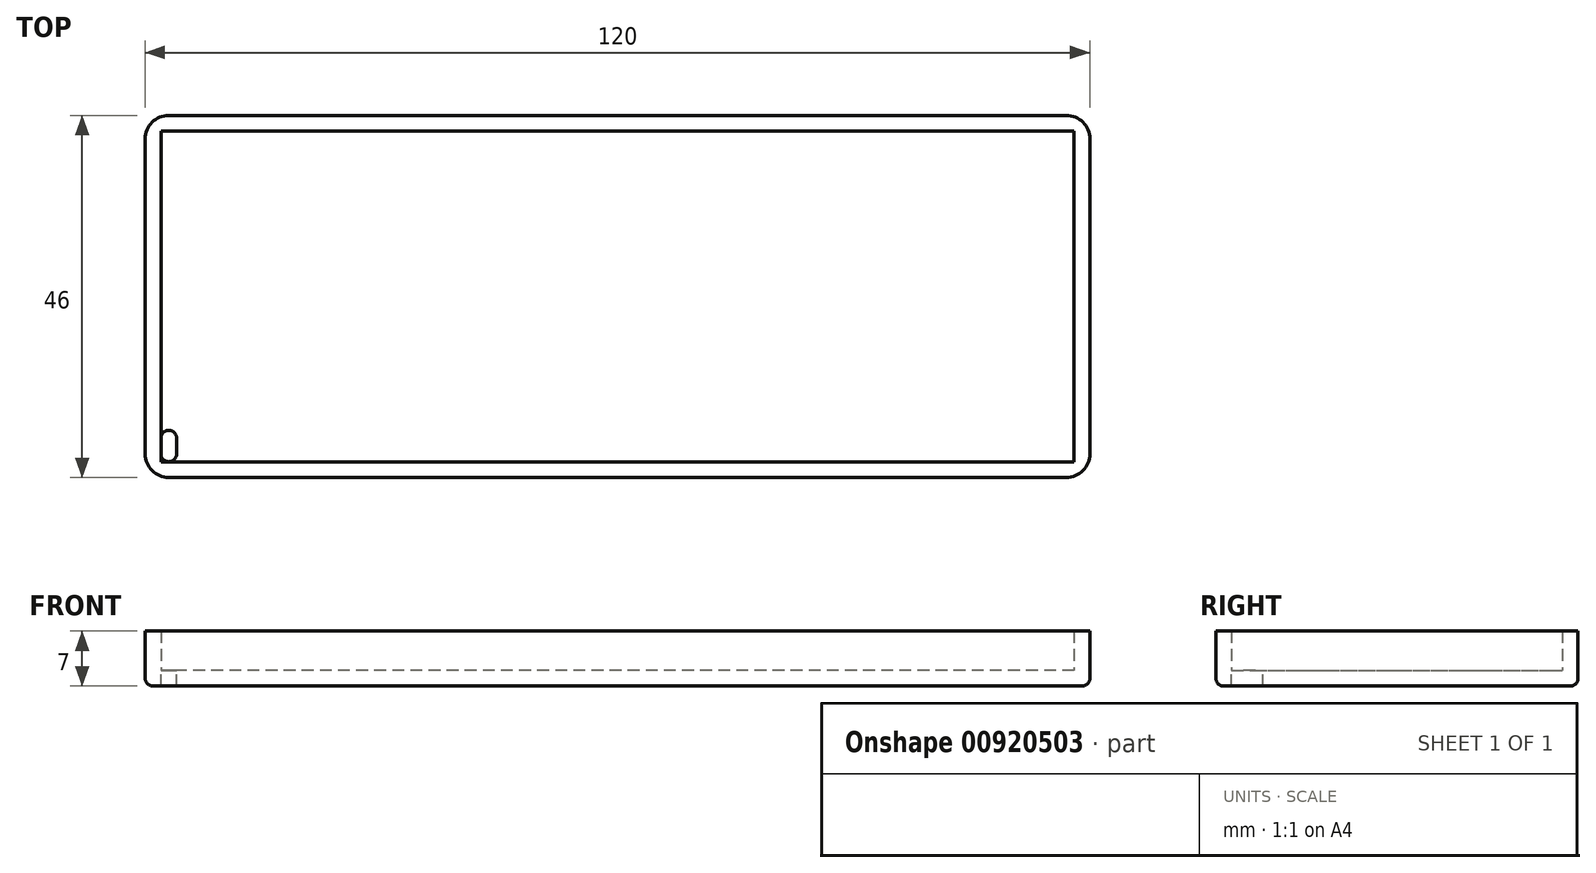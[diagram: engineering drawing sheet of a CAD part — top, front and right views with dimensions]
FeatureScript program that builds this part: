
annotation { "Feature Type Name" : "Feature", "Feature Type Description" : "" }
export const myFeature = defineFeature(function(context is Context, id is Id, definition is map)
    precondition{}
    {
        {
            var Q0;
            Q0=qCreatedBy(makeId("Top.planeOp"),FACE);
            var sketch = newSketch(context, id + "F0", { "sketchPlane" : qUnion([Q0])});
            skLineSegment(sketch, "E0.bottom", {"start": v(60, -23) * mm, "end": v(-60, -23) * mm});
            skLineSegment(sketch, "E0.top", {"start": v(60, 23) * mm, "end": v(-60, 23) * mm});
            skLineSegment(sketch, "E0.left", {"start": v(60, -23) * mm, "end": v(60, 23) * mm});
            skLineSegment(sketch, "E0.right", {"start": v(-60, -23) * mm, "end": v(-60, 23) * mm});
            skPoint(sketch, "E0.middle", {"position": v(0, 0) * mm});
            skSolve(sketch);
        }
        {
            var Q0;
            Q0=makeQuery(id+"F0.imprint","IMPRINT",FACE,{"disambiguationData":[TD([[makeQuery(id+"F0.imprint","IMPRINT",EDGE,{"derivedFrom":sQuery(id+"F0.wireOp",EDGE,"E0.bottom")}),-1.0]])]});
            extrude(context, id + "F1", {"entities" : qUnion([Q0]), "depth" : 2 * mm, "offsetDistance" : 25 * mm});
        }
        {
            var Q0;
            Q0=makeQuery(id+"F1.opExtrude","CAP_FACE",FACE,{"disambiguationData":[OSD([sQuery(id+"F0.wireOp",EDGE,"E0.bottom"),sQuery(id+"F0.wireOp",EDGE,"E0.top"),sQuery(id+"F0.wireOp",EDGE,"E0.left"),sQuery(id+"F0.wireOp",EDGE,"E0.right")])],"isStart":false});
            var sketch = newSketch(context, id + "F2", { "sketchPlane" : qUnion([Q0])});
            skLineSegment(sketch, "E1.bottom", {"start": v(58, -21) * mm, "end": v(-58, -21) * mm});
            skLineSegment(sketch, "E1.top", {"start": v(58, 21) * mm, "end": v(-58, 21) * mm});
            skLineSegment(sketch, "E1.left", {"start": v(58, -21) * mm, "end": v(58, 21) * mm});
            skLineSegment(sketch, "E1.right", {"start": v(-58, -21) * mm, "end": v(-58, 21) * mm});
            skPoint(sketch, "E1.middle", {"position": v(0, 0) * mm});
            skCircle(sketch, "E2", {"center": v(-57, -20) * mm, "radius": 1 * mm});
            skCircle(sketch, "E3", {"center": v(-57, -18) * mm, "radius": 1 * mm});
            skLineSegment(sketch, "E4", {"start": v(-56, -18) * mm, "end": v(-56, -20) * mm});
            skSolve(sketch);
        }
        {
            var Q0;
            Q0=makeQuery(id+"F2.imprint","IMPRINT",FACE,{"disambiguationData":[TD([[makeQuery(id+"F2.imprint","IMPRINT",EDGE,{"derivedFrom":sQuery(id+"F2.wireOp",EDGE,"E1.bottom")}),1.0]])]});
            extrude(context, id + "F3", {"entities" : qUnion([Q0]), "operationType" : NewBodyOperationType.ADD, "depth" : 5 * mm, "offsetDistance" : 25 * mm});
        }
        {
            var Q0;
            {var subQ0=sQuery(id+"F0.wireOp",EDGE,"E0.right");var subQ1=sQuery(id+"F0.wireOp",EDGE,"E0.top");Q0=makeQuery(id+"F3.boolean.opBoolean","MERGE",EDGE,{"derivedFrom":[makeQuery(id+"F1.opExtrude","SWEPT_EDGE",EDGE,{"disambiguationData":[OSD([subQ1,subQ0])]}),makeQuery(id+"F3.opExtrude","SWEPT_EDGE",EDGE,{"disambiguationData":[OSD([subQ1,subQ0])]})]});}
            var Q1;
            {var subQ0=sQuery(id+"F0.wireOp",EDGE,"E0.right");var subQ1=sQuery(id+"F0.wireOp",EDGE,"E0.bottom");Q1=makeQuery(id+"F3.boolean.opBoolean","MERGE",EDGE,{"derivedFrom":[makeQuery(id+"F1.opExtrude","SWEPT_EDGE",EDGE,{"disambiguationData":[OSD([subQ1,subQ0])]}),makeQuery(id+"F3.opExtrude","SWEPT_EDGE",EDGE,{"disambiguationData":[OSD([subQ1,subQ0])]})]});}
            var Q2;
            {var subQ0=sQuery(id+"F0.wireOp",EDGE,"E0.left");var subQ1=sQuery(id+"F0.wireOp",EDGE,"E0.top");Q2=makeQuery(id+"F3.boolean.opBoolean","MERGE",EDGE,{"derivedFrom":[makeQuery(id+"F1.opExtrude","SWEPT_EDGE",EDGE,{"disambiguationData":[OSD([subQ1,subQ0])]}),makeQuery(id+"F3.opExtrude","SWEPT_EDGE",EDGE,{"disambiguationData":[OSD([subQ1,subQ0])]})]});}
            var Q3;
            {var subQ0=sQuery(id+"F0.wireOp",EDGE,"E0.left");var subQ1=sQuery(id+"F0.wireOp",EDGE,"E0.bottom");Q3=makeQuery(id+"F3.boolean.opBoolean","MERGE",EDGE,{"derivedFrom":[makeQuery(id+"F1.opExtrude","SWEPT_EDGE",EDGE,{"disambiguationData":[OSD([subQ1,subQ0])]}),makeQuery(id+"F3.opExtrude","SWEPT_EDGE",EDGE,{"disambiguationData":[OSD([subQ1,subQ0])]})]});}
            fillet(context, id + "F4", {"entities" : qUnion([Q0, Q1, Q2, Q3]), "radius" : 3 * mm, "tangentPropagation" : true, "allowEdgeOverflow" : false});
        }
        {
            var Q0;
            Q0=makeQuery(id+"F1.opExtrude","CAP_EDGE",EDGE,{"disambiguationData":[OSD([sQuery(id+"F0.wireOp",EDGE,"E0.top")])],"isStart":true});
            var Q1;
            {var subQ0=sQuery(id+"F0.wireOp",EDGE,"E0.right");var subQ1=sQuery(id+"F0.wireOp",EDGE,"E0.top");Q1=makeQuery(id+"F4.opFillet","BLEND_EDGE",EDGE,{"blendedFrom":[makeQuery(id+"F3.boolean.opBoolean","MERGE",EDGE,{"derivedFrom":[makeQuery(id+"F1.opExtrude","SWEPT_EDGE",EDGE,{"disambiguationData":[OSD([subQ1,subQ0])]}),makeQuery(id+"F3.opExtrude","SWEPT_EDGE",EDGE,{"disambiguationData":[OSD([subQ1,subQ0])]})]}),makeQuery(id+"F1.opExtrude","CAP_FACE",FACE,{"disambiguationData":[OSD([sQuery(id+"F0.wireOp",EDGE,"E0.bottom"),subQ1,sQuery(id+"F0.wireOp",EDGE,"E0.left"),subQ0])],"isStart":true})],"blendedInto":[makeQuery(id+"F1.opExtrude","CAP_FACE",FACE,{"disambiguationData":[OSD([sQuery(id+"F0.wireOp",EDGE,"E0.bottom"),subQ1,sQuery(id+"F0.wireOp",EDGE,"E0.left"),subQ0])],"isStart":true})]});}
            var Q2;
            Q2=makeQuery(id+"F1.opExtrude","CAP_EDGE",EDGE,{"disambiguationData":[OSD([sQuery(id+"F0.wireOp",EDGE,"E0.right")])],"isStart":true});
            var Q3;
            {var subQ0=sQuery(id+"F0.wireOp",EDGE,"E0.right");var subQ1=sQuery(id+"F0.wireOp",EDGE,"E0.bottom");Q3=makeQuery(id+"F4.opFillet","BLEND_EDGE",EDGE,{"blendedFrom":[makeQuery(id+"F3.boolean.opBoolean","MERGE",EDGE,{"derivedFrom":[makeQuery(id+"F1.opExtrude","SWEPT_EDGE",EDGE,{"disambiguationData":[OSD([subQ1,subQ0])]}),makeQuery(id+"F3.opExtrude","SWEPT_EDGE",EDGE,{"disambiguationData":[OSD([subQ1,subQ0])]})]}),makeQuery(id+"F1.opExtrude","CAP_FACE",FACE,{"disambiguationData":[OSD([subQ1,sQuery(id+"F0.wireOp",EDGE,"E0.top"),sQuery(id+"F0.wireOp",EDGE,"E0.left"),subQ0])],"isStart":true})],"blendedInto":[makeQuery(id+"F1.opExtrude","CAP_FACE",FACE,{"disambiguationData":[OSD([subQ1,sQuery(id+"F0.wireOp",EDGE,"E0.top"),sQuery(id+"F0.wireOp",EDGE,"E0.left"),subQ0])],"isStart":true})]});}
            var Q4;
            Q4=makeQuery(id+"F1.opExtrude","CAP_EDGE",EDGE,{"disambiguationData":[OSD([sQuery(id+"F0.wireOp",EDGE,"E0.bottom")])],"isStart":true});
            var Q5;
            Q5=makeQuery(id+"F1.opExtrude","CAP_EDGE",EDGE,{"disambiguationData":[OSD([sQuery(id+"F0.wireOp",EDGE,"E0.left")])],"isStart":true});
            var Q6;
            {var subQ0=sQuery(id+"F0.wireOp",EDGE,"E0.left");var subQ1=sQuery(id+"F0.wireOp",EDGE,"E0.top");Q6=makeQuery(id+"F4.opFillet","BLEND_EDGE",EDGE,{"blendedFrom":[makeQuery(id+"F3.boolean.opBoolean","MERGE",EDGE,{"derivedFrom":[makeQuery(id+"F1.opExtrude","SWEPT_EDGE",EDGE,{"disambiguationData":[OSD([subQ1,subQ0])]}),makeQuery(id+"F3.opExtrude","SWEPT_EDGE",EDGE,{"disambiguationData":[OSD([subQ1,subQ0])]})]}),makeQuery(id+"F1.opExtrude","CAP_FACE",FACE,{"disambiguationData":[OSD([sQuery(id+"F0.wireOp",EDGE,"E0.bottom"),subQ1,subQ0,sQuery(id+"F0.wireOp",EDGE,"E0.right")])],"isStart":true})],"blendedInto":[makeQuery(id+"F1.opExtrude","CAP_FACE",FACE,{"disambiguationData":[OSD([sQuery(id+"F0.wireOp",EDGE,"E0.bottom"),subQ1,subQ0,sQuery(id+"F0.wireOp",EDGE,"E0.right")])],"isStart":true})]});}
            var Q7;
            {var subQ0=sQuery(id+"F0.wireOp",EDGE,"E0.left");var subQ1=sQuery(id+"F0.wireOp",EDGE,"E0.bottom");Q7=makeQuery(id+"F4.opFillet","BLEND_EDGE",EDGE,{"blendedFrom":[makeQuery(id+"F3.boolean.opBoolean","MERGE",EDGE,{"derivedFrom":[makeQuery(id+"F1.opExtrude","SWEPT_EDGE",EDGE,{"disambiguationData":[OSD([subQ1,subQ0])]}),makeQuery(id+"F3.opExtrude","SWEPT_EDGE",EDGE,{"disambiguationData":[OSD([subQ1,subQ0])]})]}),makeQuery(id+"F1.opExtrude","CAP_FACE",FACE,{"disambiguationData":[OSD([subQ1,sQuery(id+"F0.wireOp",EDGE,"E0.top"),subQ0,sQuery(id+"F0.wireOp",EDGE,"E0.right")])],"isStart":true})],"blendedInto":[makeQuery(id+"F1.opExtrude","CAP_FACE",FACE,{"disambiguationData":[OSD([subQ1,sQuery(id+"F0.wireOp",EDGE,"E0.top"),subQ0,sQuery(id+"F0.wireOp",EDGE,"E0.right")])],"isStart":true})]});}
            fillet(context, id + "F5", {"entities" : qUnion([Q0, Q1, Q2, Q3, Q4, Q5, Q6, Q7]), "radius" : 1 * mm, "tangentPropagation" : true, "allowEdgeOverflow" : false});
        }
        {
            var Q0;
            {var subQ0=sQuery(id+"F2.wireOp",EDGE,"E3");var subQ1=makeQuery(id+"F2.imprint","INTERSECT",VERTEX,{"derivedFrom":[subQ0,sQuery(id+"F2.wireOp",EDGE,"E4")]});Q0=makeQuery(id+"F2.imprint","IMPRINT",FACE,{"disambiguationData":[TD([[makeQuery(id+"F2.imprint","IMPRINT",EDGE,{"disambiguationData":[TD([[subQ1,-1.0]])],"derivedFrom":subQ0}),1.0]])]});}
            var Q1;
            {var subQ0=sQuery(id+"F2.wireOp",EDGE,"E4");Q1=makeQuery(id+"F2.imprint","IMPRINT",FACE,{"disambiguationData":[TD([[makeQuery(id+"F2.imprint","IMPRINT",EDGE,{"derivedFrom":subQ0}),-1.0]])]});}
            var Q2;
            {var subQ0=sQuery(id+"F2.wireOp",EDGE,"E2");var subQ1=sQuery(id+"F2.wireOp",EDGE,"E1.right");var subQ2=makeQuery(id+"F2.imprint","INTERSECT",VERTEX,{"derivedFrom":[subQ1,subQ0]});Q2=makeQuery(id+"F2.imprint","IMPRINT",FACE,{"disambiguationData":[TD([[makeQuery(id+"F2.imprint","IMPRINT",EDGE,{"disambiguationData":[TD([[subQ2,-1.0]])],"derivedFrom":subQ1}),-1.0]])]});}
            var Q3;
            {var subQ0=sQuery(id+"F2.wireOp",EDGE,"E2");var subQ1=makeQuery(id+"F2.imprint","INTERSECT",VERTEX,{"derivedFrom":[subQ0,sQuery(id+"F2.wireOp",EDGE,"E4")]});Q3=makeQuery(id+"F2.imprint","IMPRINT",FACE,{"disambiguationData":[TD([[makeQuery(id+"F2.imprint","IMPRINT",EDGE,{"disambiguationData":[TD([[subQ1,-1.0]])],"derivedFrom":subQ0}),1.0]])]});}
            extrude(context, id + "F6", {"entities" : qUnion([Q0, Q1, Q2, Q3]), "operationType" : NewBodyOperationType.REMOVE, "oppositeDirection" : true, "depth" : 25 * mm, "offsetDistance" : 25 * mm});
        }
    });
